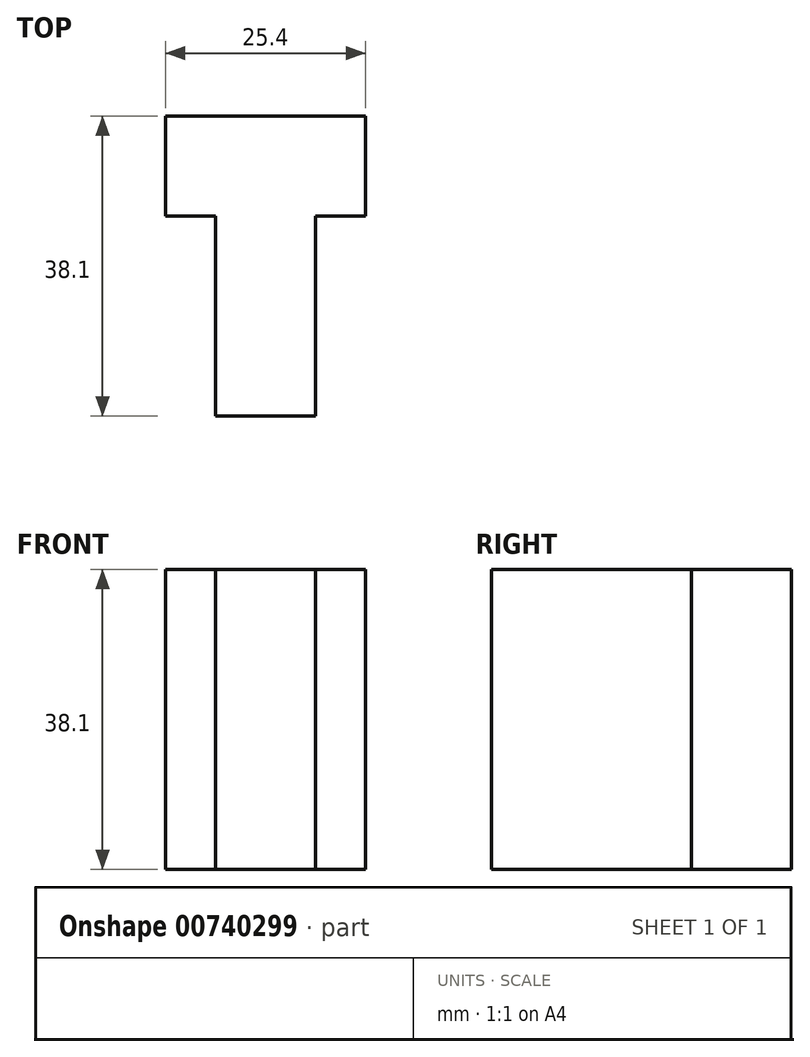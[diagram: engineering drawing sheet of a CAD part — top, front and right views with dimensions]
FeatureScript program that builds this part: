
annotation { "Feature Type Name" : "Feature", "Feature Type Description" : "" }
export const myFeature = defineFeature(function(context is Context, id is Id, definition is map)
    precondition{}
    {
        {
            var Q0;
            Q0=qCreatedBy(makeId("Top.planeOp"),FACE);
            var sketch = newSketch(context, id + "F0", { "sketchPlane" : qUnion([Q0])});
            skLineSegment(sketch, "E0", {"start": v(0, 38.1) * mm, "end": v(0, 25.4) * mm});
            skLineSegment(sketch, "E1", {"start": v(0, 25.4) * mm, "end": v(6.35, 25.4) * mm});
            skLineSegment(sketch, "E2", {"start": v(6.35, 25.4) * mm, "end": v(6.35, 0) * mm});
            skLineSegment(sketch, "E3", {"start": v(6.35, 0) * mm, "end": v(19.05, 0) * mm});
            skLineSegment(sketch, "E4", {"start": v(19.05, 0) * mm, "end": v(19.05, 25.4) * mm});
            skLineSegment(sketch, "E5", {"start": v(19.05, 25.4) * mm, "end": v(25.4, 25.4) * mm});
            skLineSegment(sketch, "E6", {"start": v(25.4, 25.4) * mm, "end": v(25.4, 38.1) * mm});
            skLineSegment(sketch, "E7", {"start": v(25.4, 38.1) * mm, "end": v(0, 38.1) * mm});
            skSolve(sketch);
        }
        {
            var Q0;
            Q0=makeQuery(id+"F0.imprint","IMPRINT",FACE,{"disambiguationData":[TD([[makeQuery(id+"F0.imprint","IMPRINT",EDGE,{"derivedFrom":sQuery(id+"F0.wireOp",EDGE,"E0")}),1.0]])]});
            extrude(context, id + "F1", {"entities" : qUnion([Q0]), "depth" : 38.1 * mm, "offsetDistance" : 25.4 * mm});
        }
    });
